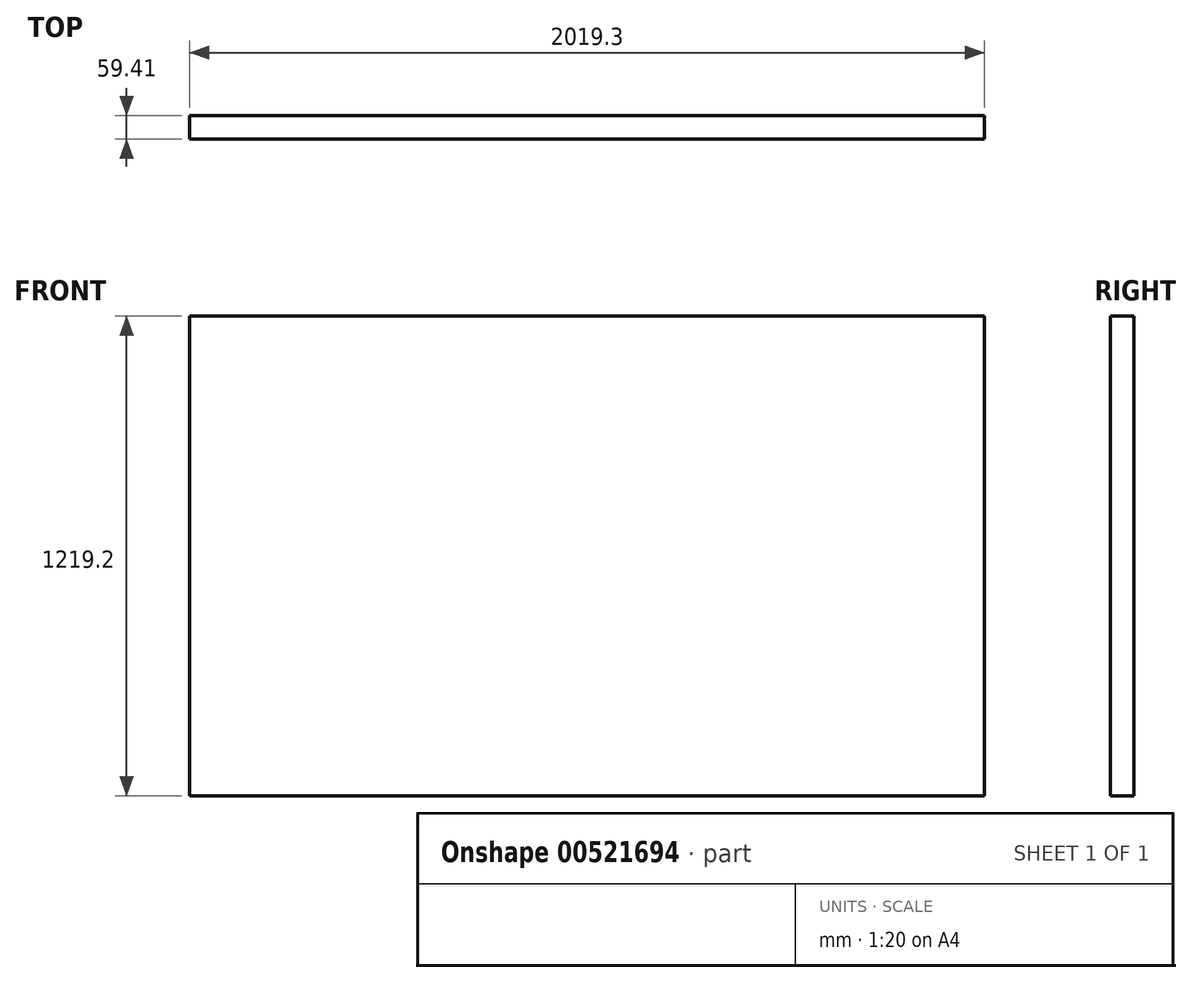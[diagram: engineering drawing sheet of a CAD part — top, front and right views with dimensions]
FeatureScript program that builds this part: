
annotation { "Feature Type Name" : "Feature", "Feature Type Description" : "" }
export const myFeature = defineFeature(function(context is Context, id is Id, definition is map)
    precondition{}
    {
        {
            var Q0;
            Q0=qCreatedBy(makeId("Front.planeOp"),FACE);
            var sketch = newSketch(context, id + "F0", { "sketchPlane" : qUnion([Q0])});
            skLineSegment(sketch, "E0.bottom", {"start": v(1009.65, 609.6) * mm, "end": v(-1009.65, 609.6) * mm});
            skLineSegment(sketch, "E0.top", {"start": v(1009.65, -609.6) * mm, "end": v(-1009.65, -609.6) * mm});
            skLineSegment(sketch, "E0.left", {"start": v(1009.65, 609.6) * mm, "end": v(1009.65, -609.6) * mm});
            skLineSegment(sketch, "E0.right", {"start": v(-1009.65, 609.6) * mm, "end": v(-1009.65, -609.6) * mm});
            skPoint(sketch, "E0.middle", {"position": v(0, 0) * mm});
            skSolve(sketch);
        }
        {
            var Q0;
            Q0 = qSketchRegion(id + "F0", true);
            extrude(context, id + "F1", {"entities" : qUnion([Q0]), "depth" : 59.4 * mm, "offsetDistance" : 25.4 * mm});
        }
    });
